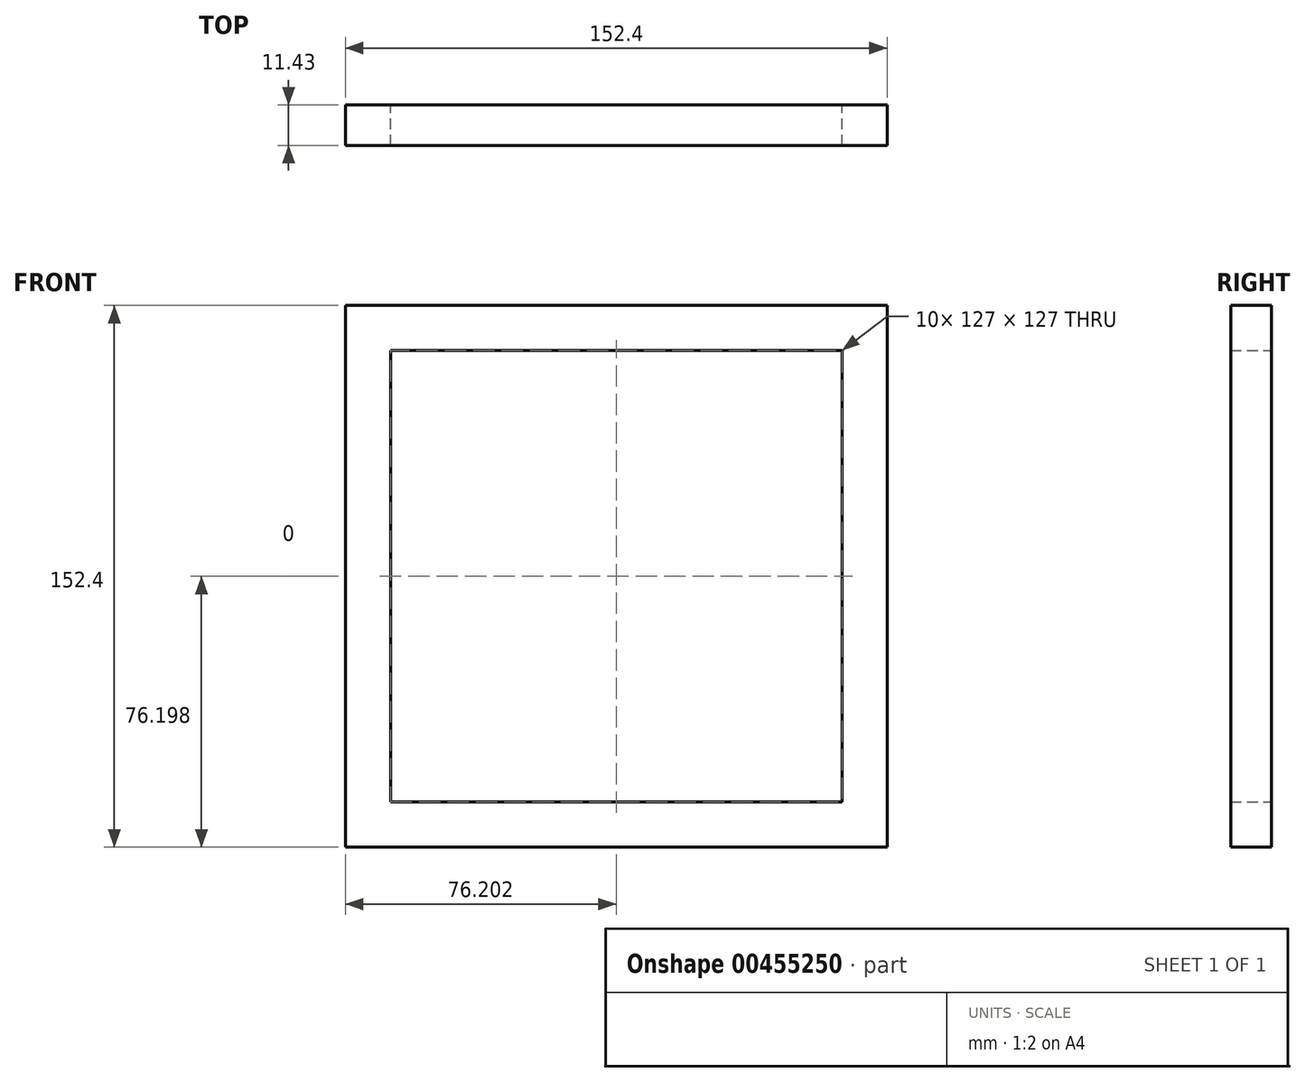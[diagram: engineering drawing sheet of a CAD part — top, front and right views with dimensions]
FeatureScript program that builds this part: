
annotation { "Feature Type Name" : "Feature", "Feature Type Description" : "" }
export const myFeature = defineFeature(function(context is Context, id is Id, definition is map)
    precondition{}
    {
        {
            var Q0;
            Q0=qCreatedBy(makeId("Front.planeOp"),FACE);
            var sketch = newSketch(context, id + "F0", { "sketchPlane" : qUnion([Q0])});
            skLineSegment(sketch, "E0.bottom", {"start": v(-90.2, 82.62) * mm, "end": v(-77.5, 82.62) * mm});
            skLineSegment(sketch, "E0.top", {"start": v(-90.2, -69.78) * mm, "end": v(-77.5, -69.78) * mm});
            skLineSegment(sketch, "E0.left", {"start": v(-90.2, 82.62) * mm, "end": v(-90.2, -69.78) * mm});
            skLineSegment(sketch, "E0.right", {"start": v(-77.5, 82.62) * mm, "end": v(-77.5, -69.78) * mm});
            skLineSegment(sketch, "E1.bottom", {"start": v(-77.5, 82.62) * mm, "end": v(49.5, 82.62) * mm});
            skLineSegment(sketch, "E1.top", {"start": v(-77.5, 69.92) * mm, "end": v(49.5, 69.92) * mm});
            skLineSegment(sketch, "E1.left", {"start": v(-77.5, 82.62) * mm, "end": v(-77.5, 69.92) * mm});
            skLineSegment(sketch, "E1.right", {"start": v(49.5, 82.62) * mm, "end": v(49.5, 69.92) * mm});
            skLineSegment(sketch, "E2.bottom", {"start": v(49.5, 82.62) * mm, "end": v(62.2, 82.62) * mm});
            skLineSegment(sketch, "E2.top", {"start": v(49.5, -69.78) * mm, "end": v(62.2, -69.78) * mm});
            skLineSegment(sketch, "E2.left", {"start": v(49.5, 82.62) * mm, "end": v(49.5, -69.78) * mm});
            skLineSegment(sketch, "E2.right", {"start": v(62.2, 82.62) * mm, "end": v(62.2, -69.78) * mm});
            skLineSegment(sketch, "E3.bottom", {"start": v(-77.5, -69.78) * mm, "end": v(49.5, -69.78) * mm});
            skLineSegment(sketch, "E3.top", {"start": v(-77.5, -57.08) * mm, "end": v(49.5, -57.08) * mm});
            skLineSegment(sketch, "E3.left", {"start": v(-77.5, -69.78) * mm, "end": v(-77.5, -57.08) * mm});
            skLineSegment(sketch, "E3.right", {"start": v(49.5, -69.78) * mm, "end": v(49.5, -57.08) * mm});
            skSolve(sketch);
        }
        {
            var Q0;
            Q0=makeQuery(id+"F0.imprint","IMPRINT",FACE,{"disambiguationData":[TD([[makeQuery(id+"F0.imprint","IMPRINT",EDGE,{"derivedFrom":sQuery(id+"F0.wireOp",EDGE,"E0.bottom")}),-1.0]])]});
            var Q1;
            {var subQ0=sQuery(id+"F0.wireOp",EDGE,"E1.bottom");Q1=makeQuery(id+"F0.imprint","IMPRINT",FACE,{"disambiguationData":[TD([[makeQuery(id+"F0.imprint","IMPRINT",EDGE,{"derivedFrom":subQ0}),-1.0]])]});}
            var Q2;
            {var subQ3=sQuery(id+"F0.wireOp",EDGE,"E2.bottom");Q2=makeQuery(id+"F0.imprint","IMPRINT",FACE,{"disambiguationData":[TD([[makeQuery(id+"F0.imprint","IMPRINT",EDGE,{"derivedFrom":subQ3}),-1.0]])]});}
            var Q3;
            Q3=makeQuery(id+"F0.imprint","IMPRINT",FACE,{"disambiguationData":[TD([[makeQuery(id+"F0.imprint","IMPRINT",EDGE,{"derivedFrom":sQuery(id+"F0.wireOp",EDGE,"E3.bottom")}),1.0]])]});
            extrude(context, id + "F1", {"entities" : qUnion([Q0, Q1, Q2, Q3]), "depth" : 11.43 * mm});
        }
    });
